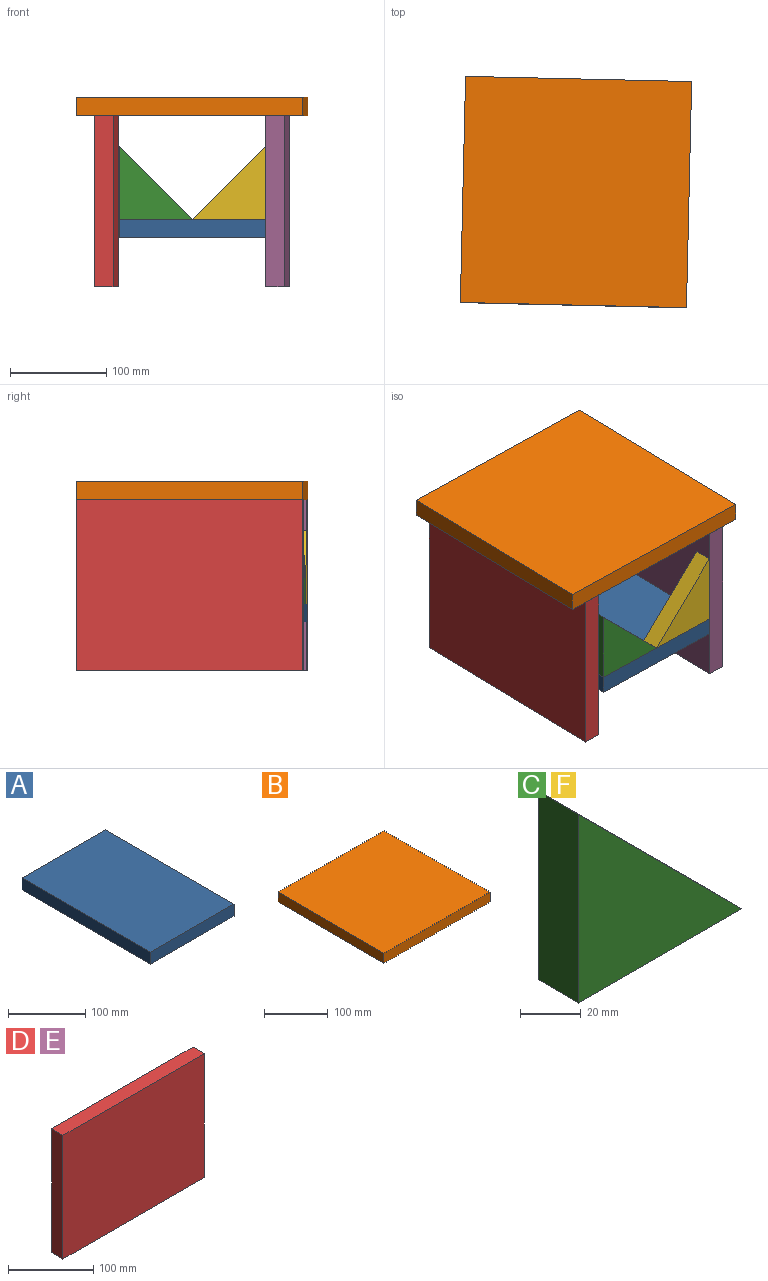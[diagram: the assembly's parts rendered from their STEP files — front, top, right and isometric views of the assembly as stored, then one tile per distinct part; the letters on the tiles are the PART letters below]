
ASSEMBLY  parts=6 mates=5
PART A: 6 faces, bbox 152.4x235x19.1 mm
  f0: plane 234.95x152.4mm, normal (0,0,1), area 35806.4mm2, adj f1,f3,f4,f5
  f1: plane 234.95x19.05mm, normal (-1,0,0), area 4475.8mm2, adj f0,f2,f4,f5
  f2: plane 234.95x152.4mm, normal (0,0,-1), area 35806.4mm2, adj f1,f3,f4,f5
  f3: plane 234.95x19.05mm, normal (1,0,0), area 4475.8mm2, adj f0,f2,f4,f5
  f4: plane 152.4x19.05mm, normal (0,-1,0), area 2903.2mm2, adj f0,f1,f2,f3
  f5: plane 152.4x19.05mm, normal (0,1,0), area 2903.2mm2, adj f0,f1,f2,f3
PART B: 6 faces, bbox 235x235x19.1 mm
  f0: plane 234.95x234.95mm, normal (0,0,1), area 55201.5mm2, adj f1,f3,f4,f5
  f1: plane 234.95x19.05mm, normal (-1,0,0), area 4475.8mm2, adj f0,f2,f4,f5
  f2: plane 234.95x234.95mm, normal (0,0,-1), area 55201.5mm2, adj f1,f3,f4,f5
  f3: plane 234.95x19.05mm, normal (1,0,0), area 4475.8mm2, adj f0,f2,f4,f5
  f4: plane 234.95x19.05mm, normal (0,-1,0), area 4475.8mm2, adj f0,f1,f2,f3
  f5: plane 234.95x19.05mm, normal (0,1,0), area 4475.8mm2, adj f0,f1,f2,f3
PART C: 5 faces, bbox 76.2x19.1x76.2 mm
  f0: plane 76.2x76.2mm, normal (0.71,0,0.71), area 2052.9mm2, adj f1,f2,f3,f4
  f1: plane 76.2x19.05mm, normal (-1,0,0), area 1451.6mm2, adj f0,f2,f3,f4
  f2: plane 76.2x19.05mm, normal (0,0,-1), area 1451.6mm2, adj f0,f1,f3,f4
  f3: plane 76.2x76.2mm, normal (0,-1,0), area 2903.2mm2, adj f0,f1,f2
  f4: plane 76.2x76.2mm, normal (0,1,0), area 2903.2mm2, adj f0,f1,f2
PART D: 6 faces, bbox 235x19.1x177.8 mm
  f0: plane 234.95x19.05mm, normal (0,0,1), area 4475.8mm2, adj f1,f3,f4,f5
  f1: plane 177.8x19.05mm, normal (-1,0,0), area 3387.1mm2, adj f0,f2,f4,f5
  f2: plane 234.95x19.05mm, normal (0,0,-1), area 4475.8mm2, adj f1,f3,f4,f5
  f3: plane 177.8x19.05mm, normal (1,0,0), area 3387.1mm2, adj f0,f2,f4,f5
  f4: plane 234.95x177.8mm, normal (0,-1,0), area 41774.1mm2, adj f0,f1,f2,f3
  f5: plane 234.95x177.8mm, normal (0,1,0), area 41774.1mm2, adj f0,f1,f2,f3
PART E: same geometry as D
PART F: same geometry as C
PLACE A rot(axis=(0,0,-1),1.3deg) t=(262.63,4.99,-194.93)mm
PLACE B rot(axis=(0,0,-1),1.3deg) t=(193.62,6.58,-69.73)mm
PLACE C rot(axis=(0,0,-1),1.3deg) t=(208.15,-209.71,-133.97)mm
PLACE D rot(axis=(0.7,-0.72,0),180deg) t=(109.53,-79.14,-153.37)mm
PLACE E rot(axis=(0.7,-0.72,0),180deg) t=(287.29,-83.23,-153.37)mm
PLACE F rot(axis=(0,0,1),178.7deg) t=(207.72,-228.76,-133.97)mm
MATE fastened C.f2 <-> A.f0  axis (0,0,-1) through (131.54,-227,-166.98)mm
MATE fastened B.f2 <-> E.f2  axis (0,0,-1) through (327.39,3.5,-59.03)mm
MATE fastened A.f3 <-> E.f5  axis (1,-0.02,0) through (283.9,-230.51,-186.03)mm
MATE fastened D.f2 <-> B.f2  axis (0,0,1) through (106.14,-226.42,-59.03)mm
MATE fastened F.f2 <-> A.f0  axis (0,0,-1) through (283.9,-230.51,-166.98)mm
